# Revit family: 510583
name_source: partatom
category: Plumbing Fixtures
revit_build: Autodesk Revit 2015 (Build: 20140606_1530(x64)
units: mm (PartAtom-declared; Revit-internal decimal feet)

## types (1)
- Type 1
    Category = Soap dispenser
    DLB090013 = Stainless Steel
    Description = French manufacturer Delabie is a leader in the European sanitary ware market for non-domestic places. Water controls, solutions for disabled people, sanitary ware, for schools, leisure centres, offices, hospitals, airports…
    Features = Liquid soap dispenser with soft-touch operation. Vandal-resistant model with lock and DELABIE standard key. One piece hinged cover for easy maintenance and improved hygiene. Soft-touch push button. Anti-blocking: one dose per push even if button is held in place. No waste, non-drip (waterproof) pump dispenser. Reservoir prevents the long-term stagnation of soap. Window for monitoring soap level. 304 stainless steel, bright polished finish. Stainless steel thickness: 1 mm. Capacity: 0.5 litre. Dimensions: 90 x 105 x 185mm. For vegetable based liquid soap with a maximum viscosity: 3,000 mPa.s.
    Finish = Bright polished
    IntegralAccessoryOptions = Hand dryer
    Manufacturer = DELABIE
    ManufacturerName = DELABIE
    Material = 304 stainless steel
    Model = Liquid soap dispenser
    Model number = 510583
    Name = 510583
    NominalHeight = 18.5cm
    NominalLength = 10.5cm
    NominalWidth = 9cm
    Operation = Soft touch
    Polantis code = DLB090013
    ProductInformation = http://www.delabie.com
    SerialNumber = 3456330169288
    Shape = Rectangle
    URL = http://www.delabie.com
    WarrantyDescription = Any manufacturing defect
    WarrantyDurationUnit = 10 years

## geometry (parser evidence)
native form markers: Sweep x3
no freeform markers — native parametric forms only
